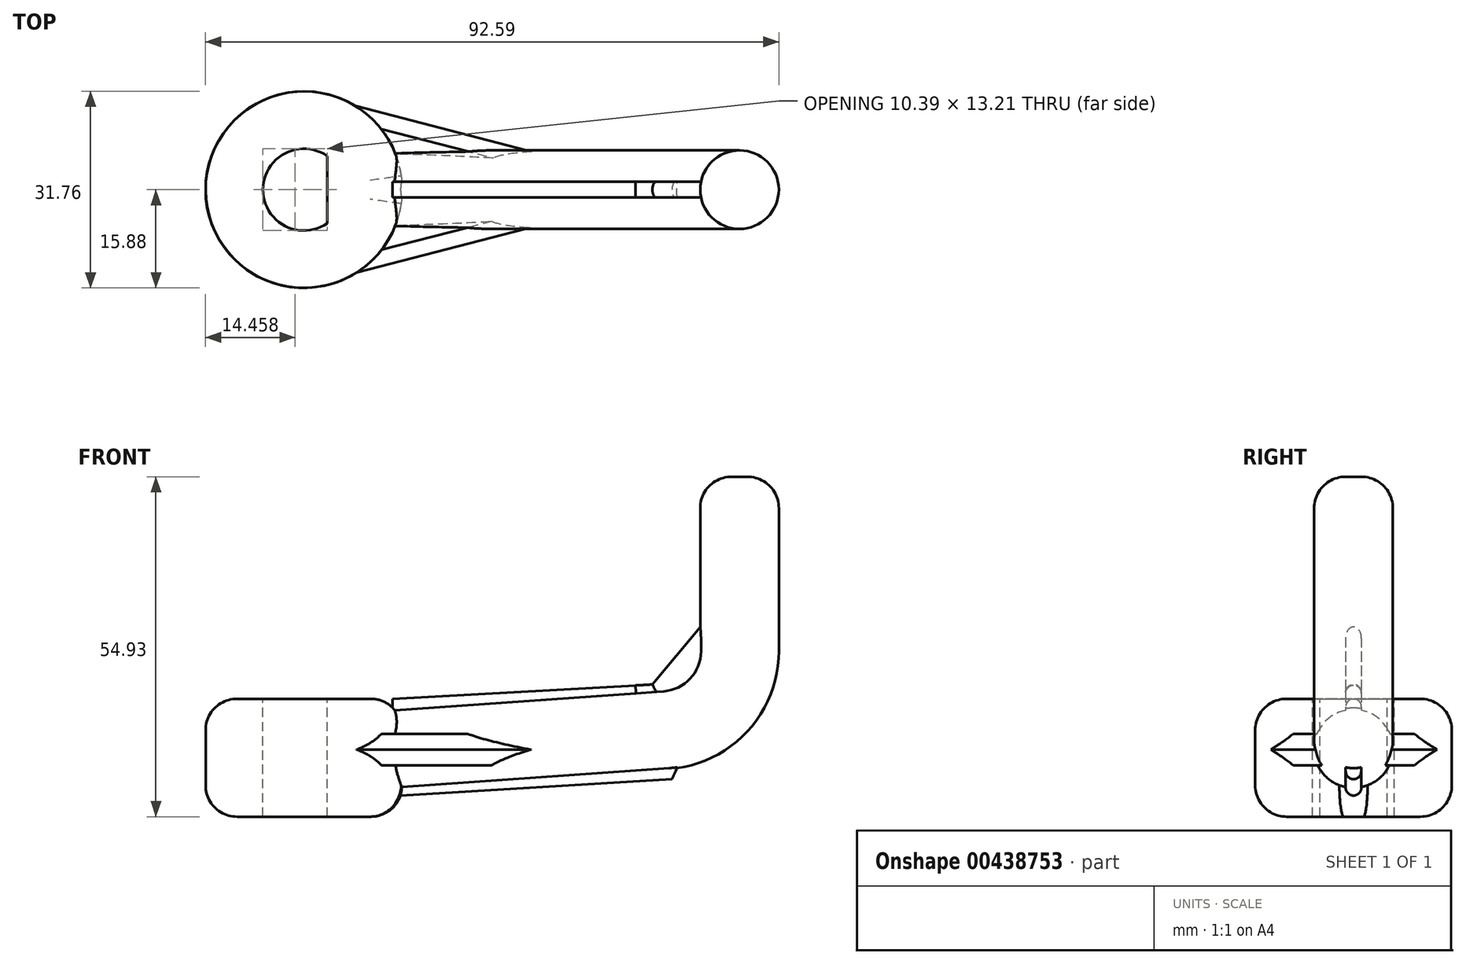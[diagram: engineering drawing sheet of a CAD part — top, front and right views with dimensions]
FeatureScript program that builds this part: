
annotation { "Feature Type Name" : "Feature", "Feature Type Description" : "" }
export const myFeature = defineFeature(function(context is Context, id is Id, definition is map)
    precondition{}
    {
        {
            var Q0;
            Q0=qCreatedBy(makeId("Top.planeOp"),FACE);
            var sketch = newSketch(context, id + "F0", { "sketchPlane" : qUnion([Q0])});
            skCircle(sketch, "E0", {"center": v(0, 0) * mm, "radius": 15.88 * mm});
            skSolve(sketch);
        }
        {
            var Q0;
            Q0=qSketchRegion(id+"F0",true);
            extrude(context, id + "F1", {"entities" : qUnion([Q0]), "depth" : 19.05 * mm});
        }
        {
            var Q0;
            Q0=makeQuery(id+"F1.opExtrude","CAP_EDGE",EDGE,{"disambiguationData":[OSD([sQuery(id+"F0.wireOp",EDGE,"E0")])],"isStart":false});
            fillet(context, id + "F2", {"entities" : qUnion([Q0]), "radius" : 5.08 * mm, "tangentPropagation" : true, "allowEdgeOverflow" : false});
        }
        {
            var Q0;
            Q0=makeQuery(id+"F1.opExtrude","CAP_FACE",FACE,{"disambiguationData":[OSD([sQuery(id+"F0.wireOp",EDGE,"E0")])],"isStart":false});
            var sketch = newSketch(context, id + "F3", { "sketchPlane" : qUnion([Q0])});
            skSolve(sketch);
        }
        {
            var Q0;
            {var subQ0=sQuery(id+"F0.wireOp",EDGE,"E0");Q0=makeQuery(id+"F3.imprint","IMPRINT",FACE,{"disambiguationData":[TD([[makeQuery(id+"F3.imprint","IMPRINT",EDGE,{"derivedFrom":makeQuery(id+"F2.opFillet","BLEND_EDGE",EDGE,{"blendedFrom":[makeQuery(id+"F1.opExtrude","CAP_EDGE",EDGE,{"disambiguationData":[OSD([subQ0])],"isStart":false}),makeQuery(id+"F1.opExtrude","CAP_FACE",FACE,{"disambiguationData":[OSD([subQ0])],"isStart":false})],"blendedInto":[makeQuery(id+"F1.opExtrude","CAP_FACE",FACE,{"disambiguationData":[OSD([subQ0])],"isStart":false})]})}),1.0]])]});}
            var sketch = newSketch(context, id + "F4", { "sketchPlane" : qUnion([Q0])});
            skArc(sketch, "E1", {"start": v(3.77, 5.44) * mm, "mid": v(-6.62, 0) * mm, "end": v(3.77, -5.44) * mm});
            skLineSegment(sketch, "E2", {"start": v(3.77, -5.44) * mm, "end": v(3.77, 5.44) * mm});
            skSolve(sketch);
        }
        {
            var Q0;
            Q0=makeQuery(id+"F4.imprint","IMPRINT",FACE,{"disambiguationData":[TD([[makeQuery(id+"F4.imprint","IMPRINT",EDGE,{"derivedFrom":sQuery(id+"F4.wireOp",EDGE,"E1")}),1.0]])]});
            extrude(context, id + "F5", {"entities" : qUnion([Q0]), "operationType" : NewBodyOperationType.REMOVE, "endBound" : BoundingType.THROUGH_ALL, "oppositeDirection" : true, "depth" : 25.4 * mm});
        }
        {
            var Q0;
            Q0=qCreatedBy(makeId("Right.planeOp"),FACE);
            cPlane(context, id + "F6", {"entities" : qUnion([Q0]), "cplaneType" : CPlaneType.OFFSET, "offset" : 13.2 * mm, "width" : 152.4 * mm, "height" : 152.4 * mm});
        }
        {
            var Q0;
            Q0=qCreatedBy(makeId("Front.planeOp"),FACE);
            var sketch = newSketch(context, id + "F7", { "sketchPlane" : qUnion([Q0])});
            skLineSegment(sketch, "E3", {"start": v(0, 0) * mm, "end": v(95.25, 0) * mm, "construction": true});
            skLineSegment(sketch, "E4", {"start": v(13.2, 0) * mm, "end": v(13.2, 17.68) * mm, "construction": true});
            skLineSegment(sketch, "E5", {"start": v(13.2, 10.85) * mm, "end": v(58.55, 14.05) * mm});
            skLineSegment(sketch, "E6", {"start": v(70.36, 26.72) * mm, "end": v(70.36, 31.3) * mm});
            skPoint(sketch, "E7.visualSharp", {"position": v(70.36, 8.84) * mm});
            skArc(sketch, "E7.filletArc", {"start": v(58.55, 14.05) * mm, "mid": v(66.95, 18.07) * mm, "end": v(70.36, 26.72) * mm});
            skSolve(sketch);
        }
        {
            var Q0;
            Q0=sQuery(id+"F7.wireOp",VERTEX,"E6.end");
            var Q1;
            Q1=qCreatedBy(makeId("Top.planeOp"),FACE);
            cPlane(context, id + "F8", {"entities" : qUnion([Q0, Q1]), "cplaneType" : CPlaneType.PLANE_POINT, "offset" : 25.4 * mm, "width" : 152.4 * mm, "height" : 152.4 * mm});
        }
        {
            var Q0;
            Q0=qCreatedBy(id+"F8.planeOp",FACE);
            var sketch = newSketch(context, id + "F9", { "sketchPlane" : qUnion([Q0])});
            skCircle(sketch, "E8", {"center": v(70.36, 0) * mm, "radius": 6.35 * mm});
            skSolve(sketch);
        }
        {
            var Q0;
            Q0=makeQuery(id+"F9.imprint","IMPRINT",FACE,{"disambiguationData":[TD([[makeQuery(id+"F9.imprint","IMPRINT",EDGE,{"derivedFrom":sQuery(id+"F9.wireOp",EDGE,"E8")}),1.0]])]});
            var Q1;
            Q1=sQuery(id+"F7.wireOp",EDGE,"E7.filletArc");
            var Q2;
            Q2=sQuery(id+"F7.wireOp",EDGE,"E5");
            var Q3;
            Q3=sQuery(id+"F7.wireOp",EDGE,"E6");
            sweep(context, id + "F10", {"operationType" : NewBodyOperationType.ADD, "profiles" : qUnion([Q0]), "path" : qUnion([Q1, Q2, Q3])});
        }
        {
            var Q0;
            Q0=makeQuery(id+"F10.opSweep","CAP_FACE",FACE,{"disambiguationData":[OSD([sQuery(id+"F7.wireOp",VERTEX,"E6.end"),sQuery(id+"F9.wireOp",EDGE,"E8")])],"isStart":true});
            extrude(context, id + "F11", {"entities" : qUnion([Q0]), "operationType" : NewBodyOperationType.ADD, "depth" : 10.92 * mm});
        }
        {
            var Q0;
            Q0=makeQuery(id+"F11.opExtrude","CAP_FACE",FACE,{"disambiguationData":[OSD([sQuery(id+"F7.wireOp",VERTEX,"E6.end"),sQuery(id+"F9.wireOp",EDGE,"E8")])],"isStart":false});
            extrude(context, id + "F12", {"entities" : qUnion([Q0]), "operationType" : NewBodyOperationType.ADD, "depth" : 12.7 * mm});
        }
        {
            var Q0;
            Q0=makeQuery(id+"F12.opExtrude","CAP_EDGE",EDGE,{"disambiguationData":[OSD([sQuery(id+"F7.wireOp",VERTEX,"E6.end"),sQuery(id+"F9.wireOp",EDGE,"E8")])],"isStart":false});
            fillet(context, id + "F13", {"entities" : qUnion([Q0]), "radius" : 5.08 * mm, "tangentPropagation" : true, "allowEdgeOverflow" : false});
        }
        {
            var Q0;
            Q0=qCreatedBy(makeId("Top.planeOp"),FACE);
            var Q1;
            Q1=sQuery(id+"F7.wireOp",VERTEX,"E5.start");
            cPlane(context, id + "F14", {"entities" : qUnion([Q0, Q1]), "cplaneType" : CPlaneType.PLANE_POINT, "offset" : 25.4 * mm, "width" : 152.4 * mm, "height" : 152.4 * mm});
        }
        {
            var Q0;
            Q0=qCreatedBy(id+"F14.planeOp",FACE);
            var sketch = newSketch(context, id + "F15", { "sketchPlane" : qUnion([Q0])});
            skLineSegment(sketch, "E9", {"start": v(60.4, 0) * mm, "end": v(6.3, 14.04) * mm});
            skLineSegment(sketch, "E10", {"start": v(6.3, 14.04) * mm, "end": v(6.3, -13.96) * mm});
            skLineSegment(sketch, "E11", {"start": v(6.3, -13.96) * mm, "end": v(60.4, 0) * mm});
            skSolve(sketch);
        }
        {
            var Q0;
            Q0=makeQuery(id+"F15.imprint","IMPRINT",FACE,{"disambiguationData":[TD([[makeQuery(id+"F15.imprint","IMPRINT",EDGE,{"derivedFrom":sQuery(id+"F15.wireOp",EDGE,"E9")}),1.0]])]});
            extrude(context, id + "F16", {"entities" : qUnion([Q0]), "operationType" : NewBodyOperationType.ADD, "depth" : 2.54 * mm, "hasSecondDirection" : true, "secondDirectionOppositeDirection" : true, "secondDirectionDepth" : 2.54 * mm});
        }
        {
            var Q0;
            Q0=makeQuery(id+"F1.opExtrude","CAP_EDGE",EDGE,{"disambiguationData":[OSD([sQuery(id+"F0.wireOp",EDGE,"E0")])],"isStart":true});
            fillet(context, id + "F17", {"entities" : qUnion([Q0]), "radius" : 5.08 * mm, "tangentPropagation" : true, "allowEdgeOverflow" : false});
        }
        {
            var Q0;
            Q0=makeQuery(id+"F16.opExtrude","CAP_EDGE",EDGE,{"disambiguationData":[OSD([sQuery(id+"F15.wireOp",EDGE,"E11")])],"isStart":false});
            var Q1;
            Q1=makeQuery(id+"F16.opExtrude","CAP_EDGE",EDGE,{"disambiguationData":[OSD([sQuery(id+"F15.wireOp",EDGE,"E11")])],"isStart":true});
            var Q2;
            Q2=makeQuery(id+"F16.opExtrude","CAP_EDGE",EDGE,{"disambiguationData":[OSD([sQuery(id+"F15.wireOp",EDGE,"E9")])],"isStart":false});
            var Q3;
            Q3=makeQuery(id+"F16.opExtrude","CAP_EDGE",EDGE,{"disambiguationData":[OSD([sQuery(id+"F15.wireOp",EDGE,"E9")])],"isStart":true});
            chamfer(context, id + "F18", {"entities" : qUnion([Q0, Q1, Q2, Q3]), "width" : 2.54 * mm, "tangentPropagation" : true});
        }
        {
            var Q0;
            Q0=qCreatedBy(makeId("Front.planeOp"),FACE);
            var sketch = newSketch(context, id + "F19", { "sketchPlane" : qUnion([Q0])});
            skLineSegment(sketch, "E12", {"start": v(14.34, 19.02) * mm, "end": v(14.34, 3.34) * mm});
            skLineSegment(sketch, "E13", {"start": v(14.34, 3.34) * mm, "end": v(59.46, 6.06) * mm});
            skLineSegment(sketch, "E14", {"start": v(59.46, 6.06) * mm, "end": v(70.4, 31.33) * mm});
            skLineSegment(sketch, "E15", {"start": v(70.4, 31.33) * mm, "end": v(64.57, 31.33) * mm});
            skLineSegment(sketch, "E16", {"start": v(64.57, 31.33) * mm, "end": v(56.3, 21.36) * mm});
            skLineSegment(sketch, "E17", {"start": v(56.3, 21.36) * mm, "end": v(14.34, 19.02) * mm});
            skSolve(sketch);
        }
        {
            var Q0;
            Q0=makeQuery(id+"F19.imprint","IMPRINT",FACE,{"disambiguationData":[TD([[makeQuery(id+"F19.imprint","IMPRINT",EDGE,{"derivedFrom":sQuery(id+"F19.wireOp",EDGE,"E12")}),1.0]])]});
            extrude(context, id + "F20", {"entities" : qUnion([Q0]), "operationType" : NewBodyOperationType.ADD, "depth" : 1.27 * mm, "hasSecondDirection" : true, "secondDirectionOppositeDirection" : true, "secondDirectionDepth" : 1.27 * mm});
        }
        {
            var Q0;
            Q0=makeQuery(id+"F20.opExtrude","CAP_EDGE",EDGE,{"disambiguationData":[OSD([sQuery(id+"F19.wireOp",EDGE,"E16")])],"isStart":false});
            var Q1;
            Q1=makeQuery(id+"F20.opExtrude","CAP_EDGE",EDGE,{"disambiguationData":[OSD([sQuery(id+"F19.wireOp",EDGE,"E16")])],"isStart":true});
            var Q2;
            Q2=makeQuery(id+"F20.opExtrude","CAP_EDGE",EDGE,{"disambiguationData":[OSD([sQuery(id+"F19.wireOp",EDGE,"E13")])],"isStart":false});
            var Q3;
            Q3=makeQuery(id+"F20.opExtrude","CAP_EDGE",EDGE,{"disambiguationData":[OSD([sQuery(id+"F19.wireOp",EDGE,"E17")])],"isStart":false});
            var Q4;
            Q4=makeQuery(id+"F20.opExtrude","CAP_EDGE",EDGE,{"disambiguationData":[OSD([sQuery(id+"F19.wireOp",EDGE,"E17")])],"isStart":true});
            var Q5;
            Q5=makeQuery(id+"F20.opExtrude","CAP_EDGE",EDGE,{"disambiguationData":[OSD([sQuery(id+"F19.wireOp",EDGE,"E13")])],"isStart":true});
            fillet(context, id + "F21", {"entities" : qUnion([Q0, Q1, Q2, Q3, Q4, Q5]), "radius" : 1.27 * mm, "tangentPropagation" : true, "allowEdgeOverflow" : false});
        }
    });
